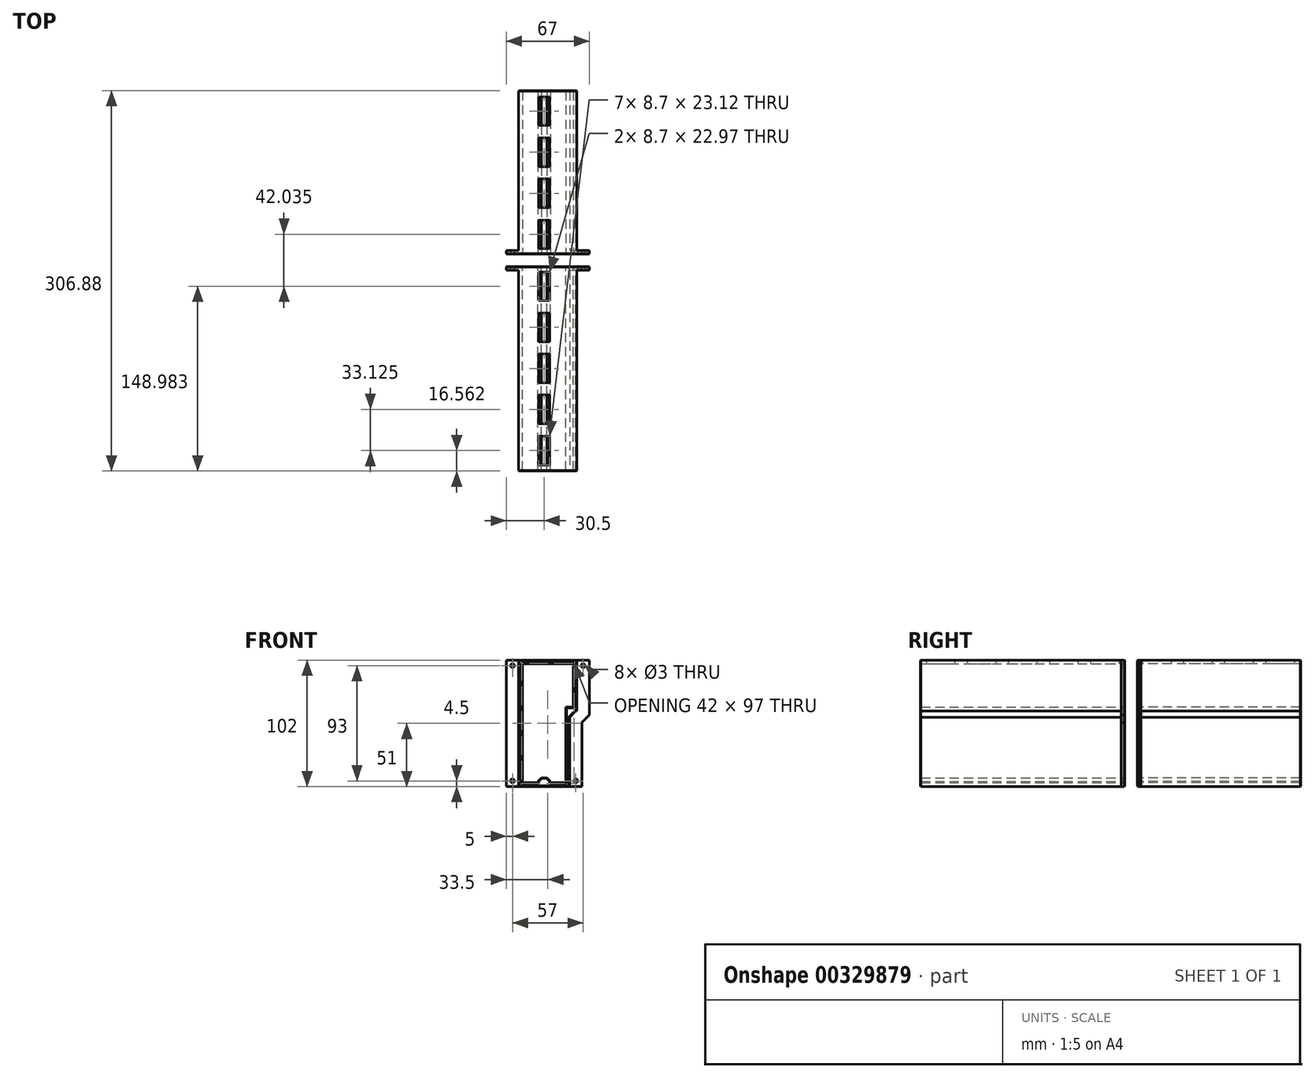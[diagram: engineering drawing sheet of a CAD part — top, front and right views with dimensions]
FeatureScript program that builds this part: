
annotation { "Feature Type Name" : "Feature", "Feature Type Description" : "" }
export const myFeature = defineFeature(function(context is Context, id is Id, definition is map)
    precondition{}
    {
        {
            var Q0;
            Q0=qCreatedBy(makeId("Front.planeOp"),FACE);
            var sketch = newSketch(context, id + "F0", { "sketchPlane" : qUnion([Q0])});
            skLineSegment(sketch, "E0", {"start": v(0, 0) * mm, "end": v(0, 1.2) * mm});
            skLineSegment(sketch, "E1", {"start": v(0, 1.2) * mm, "end": v(2.9, 4.1) * mm});
            skLineSegment(sketch, "E2", {"start": v(2.9, 4.1) * mm, "end": v(5, 4.1) * mm});
            skLineSegment(sketch, "E3", {"start": v(5, 4.1) * mm, "end": v(5, 0) * mm, "construction": true});
            skLineSegment(sketch, "E4", {"start": v(5, 0) * mm, "end": v(0, 0) * mm, "construction": true});
            skLineSegment(sketch, "E5", {"start": v(0, 0) * mm, "end": v(-12.5, 0) * mm});
            skLineSegment(sketch, "E6", {"start": v(-12.5, 0) * mm, "end": v(-12.5, 96) * mm});
            skLineSegment(sketch, "E7", {"start": v(-12.5, 96) * mm, "end": v(0.65, 96) * mm});
            skLineSegment(sketch, "E8", {"start": v(0.65, 96) * mm, "end": v(0.65, 99) * mm});
            skLineSegment(sketch, "E9", {"start": v(0.65, 99) * mm, "end": v(-15.5, 99) * mm});
            skLineSegment(sketch, "E10", {"start": v(-15.5, 99) * mm, "end": v(-15.5, -3) * mm});
            skLineSegment(sketch, "E11", {"start": v(-15.5, -3) * mm, "end": v(5, -3) * mm});
            skLineSegment(sketch, "E12", {"start": v(5, -3) * mm, "end": v(5, 0) * mm, "construction": true});
            skLineSegment(sketch, "E13.MirrorCS", {"start": v(7.1, 4.1) * mm, "end": v(5, 4.1) * mm});
            skLineSegment(sketch, "E14.MirrorCS", {"start": v(10, 1.2) * mm, "end": v(7.1, 4.1) * mm});
            skLineSegment(sketch, "E15.MirrorCS", {"start": v(10, 0) * mm, "end": v(10, 1.2) * mm});
            skLineSegment(sketch, "E16.MirrorCS", {"start": v(10, 0) * mm, "end": v(22.5, 0) * mm});
            skLineSegment(sketch, "E17.MirrorCS", {"start": v(22.5, 0) * mm, "end": v(22.5, 61) * mm});
            skLineSegment(sketch, "E18.MirrorCS", {"start": v(25.5, -3) * mm, "end": v(5, -3) * mm});
            skLineSegment(sketch, "E19.MirrorCS", {"start": v(9.35, 99) * mm, "end": v(31.5, 99) * mm});
            skLineSegment(sketch, "E20.MirrorCS", {"start": v(22.5, 96) * mm, "end": v(9.35, 96) * mm});
            skLineSegment(sketch, "E21.MirrorCS", {"start": v(9.35, 96) * mm, "end": v(9.35, 99) * mm});
            skLineSegment(sketch, "E22", {"start": v(22.5, 61) * mm, "end": v(28.5, 61) * mm});
            skLineSegment(sketch, "E23", {"start": v(28.5, 61) * mm, "end": v(28.5, 96) * mm});
            skLineSegment(sketch, "E24", {"start": v(28.5, 96) * mm, "end": v(22.5, 96) * mm});
            skLineSegment(sketch, "E25.0", {"start": v(31.5, 58) * mm, "end": v(31.5, 99) * mm});
            skLineSegment(sketch, "E25.1", {"start": v(25.5, 58) * mm, "end": v(31.5, 58) * mm});
            skLineSegment(sketch, "E25.2", {"start": v(25.5, -3) * mm, "end": v(25.5, 58) * mm});
            skSolve(sketch);
        }
        {
            var Q0;
            Q0 = qSketchRegion(id + "F0", true);
            extrude(context, id + "F1", {"entities" : qUnion([Q0]), "depth" : 165 * mm, "offsetDistance" : 25 * mm});
        }
        {
            var Q0;
            Q0=makeQuery(id+"F1.opExtrude","SWEPT_FACE",FACE,{"disambiguationData":[OSD([sQuery(id+"F0.wireOp",EDGE,"E9")])]});
            var sketch = newSketch(context, id + "F2", { "sketchPlane" : qUnion([Q0])});
            skLineSegment(sketch, "E26.bottom", {"start": v(0.65, -165) * mm, "end": v(9.35, -165) * mm});
            skLineSegment(sketch, "E26.top", {"start": v(0.65, -160) * mm, "end": v(9.35, -160) * mm});
            skLineSegment(sketch, "E26.left", {"start": v(0.65, -165) * mm, "end": v(0.65, -160) * mm});
            skLineSegment(sketch, "E26.right", {"start": v(9.35, -165) * mm, "end": v(9.35, -160) * mm});
            skLineSegment(sketch, "E27", {"start": v(0.65, -148.44) * mm, "end": v(9.35, -148.44) * mm, "construction": true});
            skLineSegment(sketch, "E28.bottom", {"start": v(0.65, -136.88) * mm, "end": v(9.35, -136.88) * mm});
            skLineSegment(sketch, "E28.top", {"start": v(0.65, -126.87) * mm, "end": v(9.35, -126.87) * mm});
            skLineSegment(sketch, "E28.left", {"start": v(0.65, -136.88) * mm, "end": v(0.65, -126.87) * mm});
            skLineSegment(sketch, "E28.right", {"start": v(9.35, -136.88) * mm, "end": v(9.35, -126.87) * mm});
            skLineSegment(sketch, "E29.0.1.0", {"start": v(0.65, -115.31) * mm, "end": v(9.35, -115.31) * mm, "construction": true});
            skLineSegment(sketch, "E29.0.1.1", {"start": v(0.65, -103.75) * mm, "end": v(9.35, -103.75) * mm});
            skLineSegment(sketch, "E29.0.1.2", {"start": v(0.65, -103.75) * mm, "end": v(0.65, -93.75) * mm});
            skLineSegment(sketch, "E29.0.1.3", {"start": v(0.65, -93.75) * mm, "end": v(9.35, -93.75) * mm});
            skLineSegment(sketch, "E29.0.1.4", {"start": v(9.35, -103.75) * mm, "end": v(9.35, -93.75) * mm});
            skLineSegment(sketch, "E29.direction2", {"start": v(0.65, -148.44) * mm, "end": v(0.65, -115.31) * mm, "construction": true});
            skLineSegment(sketch, "E30", {"start": v(0.65, -131.88) * mm, "end": v(0.65, -115.31) * mm});
            skLineSegment(sketch, "E31", {"start": v(0.65, -131.88) * mm, "end": v(0.65, -148.44) * mm});
            skLineSegment(sketch, "E32.0.0.2", {"start": v(0.65, -82.19) * mm, "end": v(9.35, -82.19) * mm, "construction": true});
            skLineSegment(sketch, "E32.3.0.2", {"start": v(0.65, -70.63) * mm, "end": v(9.35, -70.63) * mm});
            skLineSegment(sketch, "E32.6.0.2", {"start": v(0.65, -70.63) * mm, "end": v(0.65, -60.63) * mm});
            skLineSegment(sketch, "E32.9.0.2", {"start": v(0.65, -60.63) * mm, "end": v(9.35, -60.63) * mm});
            skLineSegment(sketch, "E32.12.0.2", {"start": v(9.35, -70.63) * mm, "end": v(9.35, -60.63) * mm});
            skLineSegment(sketch, "E32.0.0.3", {"start": v(0.65, -49.06) * mm, "end": v(9.35, -49.06) * mm, "construction": true});
            skLineSegment(sketch, "E32.3.0.3", {"start": v(0.65, -37.5) * mm, "end": v(9.35, -37.5) * mm});
            skLineSegment(sketch, "E32.6.0.3", {"start": v(0.65, -37.5) * mm, "end": v(0.65, -27.5) * mm});
            skLineSegment(sketch, "E32.9.0.3", {"start": v(0.65, -27.5) * mm, "end": v(9.35, -27.5) * mm});
            skLineSegment(sketch, "E32.12.0.3", {"start": v(9.35, -37.5) * mm, "end": v(9.35, -27.5) * mm});
            skLineSegment(sketch, "E33.0.0.4", {"start": v(0.65, -15.94) * mm, "end": v(9.35, -15.94) * mm, "construction": true});
            skLineSegment(sketch, "E33.3.0.4", {"start": v(0.65, -4.53) * mm, "end": v(9.35, -4.53) * mm});
            skLineSegment(sketch, "E33.6.0.4", {"start": v(0.65, -4.53) * mm, "end": v(0.65, 0) * mm});
            skLineSegment(sketch, "E33.9.0.4", {"start": v(0.65, 0) * mm, "end": v(9.35, 0) * mm});
            skLineSegment(sketch, "E33.12.0.4", {"start": v(9.35, -4.53) * mm, "end": v(9.35, 0) * mm});
            skSolve(sketch);
        }
        {
            var Q0;
            Q0 = qSketchRegion(id + "F2", true);
            var Q1;
            Q1=makeQuery(id+"F1.opExtrude","SWEPT_FACE",FACE,{"disambiguationData":[OSD([sQuery(id+"F0.wireOp",EDGE,"E7")])]});
            extrude(context, id + "F3", {"entities" : qUnion([Q0]), "operationType" : NewBodyOperationType.ADD, "endBound" : BoundingType.UP_TO_SURFACE, "oppositeDirection" : true, "depth" : 25 * mm, "endBoundEntityFace" : qUnion([Q1]), "offsetDistance" : 25 * mm});
        }
        {
            var Q0;
            Q0=makeQuery(id+"F1.opExtrude","SWEPT_EDGE",EDGE,{"disambiguationData":[OSD([sQuery(id+"F0.wireOp",EDGE,"E25.1"),sQuery(id+"F0.wireOp",EDGE,"E25.2")])]});
            chamfer(context, id + "F4", {"entities" : qUnion([Q0]), "width" : 5 * mm, "tangentPropagation" : true});
        }
        {
            var Q0;
            Q0=makeQuery(id+"F3.boolean.opBoolean","MERGE",FACE,{"derivedFrom":[makeQuery(id+"F1.opExtrude","CAP_FACE",FACE,{"disambiguationData":[OSD([sQuery(id+"F0.wireOp",EDGE,"E0"),sQuery(id+"F0.wireOp",EDGE,"E1"),sQuery(id+"F0.wireOp",EDGE,"E2"),sQuery(id+"F0.wireOp",EDGE,"E5"),sQuery(id+"F0.wireOp",EDGE,"E6"),sQuery(id+"F0.wireOp",EDGE,"E7"),sQuery(id+"F0.wireOp",EDGE,"E8"),sQuery(id+"F0.wireOp",EDGE,"E9"),sQuery(id+"F0.wireOp",EDGE,"E10"),sQuery(id+"F0.wireOp",EDGE,"E11"),sQuery(id+"F0.wireOp",EDGE,"E13.MirrorCS"),sQuery(id+"F0.wireOp",EDGE,"E14.MirrorCS"),sQuery(id+"F0.wireOp",EDGE,"E15.MirrorCS"),sQuery(id+"F0.wireOp",EDGE,"E16.MirrorCS"),sQuery(id+"F0.wireOp",EDGE,"E17.MirrorCS"),sQuery(id+"F0.wireOp",EDGE,"E18.MirrorCS"),sQuery(id+"F0.wireOp",EDGE,"E19.MirrorCS"),sQuery(id+"F0.wireOp",EDGE,"E20.MirrorCS"),sQuery(id+"F0.wireOp",EDGE,"E21.MirrorCS"),sQuery(id+"F0.wireOp",EDGE,"E22"),sQuery(id+"F0.wireOp",EDGE,"E23"),sQuery(id+"F0.wireOp",EDGE,"E24"),sQuery(id+"F0.wireOp",EDGE,"E25.0"),sQuery(id+"F0.wireOp",EDGE,"E25.1"),sQuery(id+"F0.wireOp",EDGE,"E25.2")])],"isStart":true}),makeQuery(id+"F3.opExtrude","SWEPT_FACE",FACE,{"disambiguationData":[OSD([sQuery(id+"F2.wireOp",EDGE,"E33.9.0.4")])]})]});
            var sketch = newSketch(context, id + "F5", { "sketchPlane" : qUnion([Q0])});
            skLineSegment(sketch, "E34.0", {"start": v(-22.5, 61) * mm, "end": v(-28.5, 61) * mm});
            skLineSegment(sketch, "E34.1", {"start": v(0, 0) * mm, "end": v(0, 1.2) * mm});
            skLineSegment(sketch, "E34.2", {"start": v(0, 0) * mm, "end": v(12.5, 0) * mm});
            skLineSegment(sketch, "E34.3", {"start": v(12.5, 0) * mm, "end": v(12.5, 96) * mm});
            skLineSegment(sketch, "E34.4", {"start": v(-28.5, 96) * mm, "end": v(12.5, 96) * mm});
            skLineSegment(sketch, "E34.5", {"start": v(0, 1.2) * mm, "end": v(-2.9, 4.1) * mm});
            skLineSegment(sketch, "E34.6", {"start": v(-28.5, 61) * mm, "end": v(-28.5, 96) * mm});
            skLineSegment(sketch, "E34.7", {"start": v(-2.9, 4.1) * mm, "end": v(-7.1, 4.1) * mm});
            skLineSegment(sketch, "E34.8", {"start": v(-10, 1.2) * mm, "end": v(-7.1, 4.1) * mm});
            skLineSegment(sketch, "E34.9", {"start": v(-10, 0) * mm, "end": v(-10, 1.2) * mm});
            skLineSegment(sketch, "E34.10", {"start": v(-10, 0) * mm, "end": v(-22.5, 0) * mm});
            skLineSegment(sketch, "E34.11", {"start": v(-22.5, 0) * mm, "end": v(-22.5, 61) * mm});
            skLineSegment(sketch, "E35.0", {"start": v(25.5, 99) * mm, "end": v(25.5, -3) * mm});
            skLineSegment(sketch, "E35.1", {"start": v(-35.5, -3) * mm, "end": v(-35.5, 48.86) * mm});
            skLineSegment(sketch, "E35.2", {"start": v(-41.5, 54.86) * mm, "end": v(-35.5, 48.86) * mm});
            skLineSegment(sketch, "E35.3", {"start": v(-41.5, 54.86) * mm, "end": v(-41.5, 99) * mm});
            skLineSegment(sketch, "E35.4", {"start": v(25.5, 99) * mm, "end": v(-41.5, 99) * mm});
            skLineSegment(sketch, "E36", {"start": v(-35.5, -3) * mm, "end": v(25.5, -3) * mm});
            skCircle(sketch, "E37", {"center": v(-30.5, 1.5) * mm, "radius": 1.5 * mm});
            skCircle(sketch, "E38", {"center": v(-36.5, 94.5) * mm, "radius": 1.5 * mm});
            skCircle(sketch, "E39", {"center": v(20.5, 94.5) * mm, "radius": 1.5 * mm});
            skCircle(sketch, "E40", {"center": v(20.5, 1.5) * mm, "radius": 1.5 * mm});
            skLineSegment(sketch, "E41", {"start": v(-35.5, 1.5) * mm, "end": v(-30.5, 1.5) * mm, "construction": true});
            skLineSegment(sketch, "E42", {"start": v(-30.5, 1.5) * mm, "end": v(-25.5, 1.5) * mm, "construction": true});
            skLineSegment(sketch, "E43", {"start": v(15.5, 1.5) * mm, "end": v(20.5, 1.5) * mm, "construction": true});
            skLineSegment(sketch, "E44", {"start": v(20.5, 1.5) * mm, "end": v(25.5, 1.5) * mm, "construction": true});
            skLineSegment(sketch, "E45", {"start": v(-31.5, 94.5) * mm, "end": v(-41.5, 94.5) * mm, "construction": true});
            skLineSegment(sketch, "E46", {"start": v(15.5, 94.5) * mm, "end": v(25.5, 94.5) * mm, "construction": true});
            skSolve(sketch);
        }
        {
            var Q0;
            Q0 = qSketchRegion(id + "F5", true);
            extrude(context, id + "F6", {"entities" : qUnion([Q0]), "operationType" : NewBodyOperationType.ADD, "oppositeDirection" : true, "depth" : 3 * mm, "offsetDistance" : 25 * mm});
        }
        {
            var Q0;
            {var subQ0=makeQuery(id+"F1.opExtrude","CAP_FACE",FACE,{"disambiguationData":[OSD([sQuery(id+"F0.wireOp",EDGE,"E0"),sQuery(id+"F0.wireOp",EDGE,"E1"),sQuery(id+"F0.wireOp",EDGE,"E2"),sQuery(id+"F0.wireOp",EDGE,"E3"),sQuery(id+"F0.wireOp",EDGE,"E5"),sQuery(id+"F0.wireOp",EDGE,"E6"),sQuery(id+"F0.wireOp",EDGE,"E7"),sQuery(id+"F0.wireOp",EDGE,"E8"),sQuery(id+"F0.wireOp",EDGE,"E9"),sQuery(id+"F0.wireOp",EDGE,"E10"),sQuery(id+"F0.wireOp",EDGE,"E11"),sQuery(id+"F0.wireOp",EDGE,"E12")])],"isStart":true});Q0=makeQuery(id+"F2d3Ql1Mtt5XJC1_1.boolean.opBoolean","MERGE",FACE,{"derivedFrom":[subQ0,makeQuery(id+"F2d3Ql1Mtt5XJC1_1.opPattern","COPY",FACE,{"derivedFrom":subQ0,"instanceName":"1"})]});}
            var Q1;
            {var subQ0=makeQuery(id+"F1.opExtrude","CAP_FACE",FACE,{"disambiguationData":[OSD([sQuery(id+"F0.wireOp",EDGE,"E0"),sQuery(id+"F0.wireOp",EDGE,"E1"),sQuery(id+"F0.wireOp",EDGE,"E2"),sQuery(id+"F0.wireOp",EDGE,"E3"),sQuery(id+"F0.wireOp",EDGE,"E5"),sQuery(id+"F0.wireOp",EDGE,"E6"),sQuery(id+"F0.wireOp",EDGE,"E7"),sQuery(id+"F0.wireOp",EDGE,"E8"),sQuery(id+"F0.wireOp",EDGE,"E9"),sQuery(id+"F0.wireOp",EDGE,"E10"),sQuery(id+"F0.wireOp",EDGE,"E11"),sQuery(id+"F0.wireOp",EDGE,"E12")])],"isStart":false});Q1=makeQuery(id+"F2d3Ql1Mtt5XJC1_1.boolean.opBoolean","MERGE",FACE,{"derivedFrom":[subQ0,makeQuery(id+"F2d3Ql1Mtt5XJC1_1.opPattern","COPY",FACE,{"derivedFrom":subQ0,"instanceName":"1"})]});}
            chamfer(context, id + "F7", {"entities" : qUnion([Q0, Q1]), "width" : 0.5 * mm, "tangentPropagation" : true});
        }
        {
            var Q0;
            Q0=makeQuery(id+"F6.boolean.opBoolean","MERGE",FACE,{"derivedFrom":[makeQuery(id+"F3.boolean.opBoolean","MERGE",FACE,{"derivedFrom":[makeQuery(id+"F1.opExtrude","CAP_FACE",FACE,{"disambiguationData":[OSD([sQuery(id+"F0.wireOp",EDGE,"E0"),sQuery(id+"F0.wireOp",EDGE,"E1"),sQuery(id+"F0.wireOp",EDGE,"E2"),sQuery(id+"F0.wireOp",EDGE,"E5"),sQuery(id+"F0.wireOp",EDGE,"E6"),sQuery(id+"F0.wireOp",EDGE,"E7"),sQuery(id+"F0.wireOp",EDGE,"E8"),sQuery(id+"F0.wireOp",EDGE,"E9"),sQuery(id+"F0.wireOp",EDGE,"E10"),sQuery(id+"F0.wireOp",EDGE,"E11"),sQuery(id+"F0.wireOp",EDGE,"E13.MirrorCS"),sQuery(id+"F0.wireOp",EDGE,"E14.MirrorCS"),sQuery(id+"F0.wireOp",EDGE,"E15.MirrorCS"),sQuery(id+"F0.wireOp",EDGE,"E16.MirrorCS"),sQuery(id+"F0.wireOp",EDGE,"E17.MirrorCS"),sQuery(id+"F0.wireOp",EDGE,"E18.MirrorCS"),sQuery(id+"F0.wireOp",EDGE,"E19.MirrorCS"),sQuery(id+"F0.wireOp",EDGE,"E20.MirrorCS"),sQuery(id+"F0.wireOp",EDGE,"E21.MirrorCS"),sQuery(id+"F0.wireOp",EDGE,"E22"),sQuery(id+"F0.wireOp",EDGE,"E23"),sQuery(id+"F0.wireOp",EDGE,"E24"),sQuery(id+"F0.wireOp",EDGE,"E25.0"),sQuery(id+"F0.wireOp",EDGE,"E25.1"),sQuery(id+"F0.wireOp",EDGE,"E25.2")])],"isStart":true}),makeQuery(id+"F3.opExtrude","SWEPT_FACE",FACE,{"disambiguationData":[OSD([sQuery(id+"F2.wireOp",EDGE,"E33.9.0.4")])]})]}),makeQuery(id+"F6.opExtrude","CAP_FACE",FACE,{"disambiguationData":[OSD([sQuery(id+"F5.wireOp",EDGE,"E34.0"),sQuery(id+"F5.wireOp",EDGE,"E34.1"),sQuery(id+"F5.wireOp",EDGE,"E34.2"),sQuery(id+"F5.wireOp",EDGE,"E34.3"),sQuery(id+"F5.wireOp",EDGE,"E34.4"),sQuery(id+"F5.wireOp",EDGE,"E34.5"),sQuery(id+"F5.wireOp",EDGE,"E34.6"),sQuery(id+"F5.wireOp",EDGE,"E34.7"),sQuery(id+"F5.wireOp",EDGE,"E34.8"),sQuery(id+"F5.wireOp",EDGE,"E34.9"),sQuery(id+"F5.wireOp",EDGE,"E34.10"),sQuery(id+"F5.wireOp",EDGE,"E34.11"),sQuery(id+"F5.wireOp",EDGE,"E35.0"),sQuery(id+"F5.wireOp",EDGE,"E35.1"),sQuery(id+"F5.wireOp",EDGE,"E35.2"),sQuery(id+"F5.wireOp",EDGE,"E35.3"),sQuery(id+"F5.wireOp",EDGE,"E35.4"),sQuery(id+"F5.wireOp",EDGE,"E36"),sQuery(id+"F5.wireOp",EDGE,"E37"),sQuery(id+"F5.wireOp",EDGE,"E38"),sQuery(id+"F5.wireOp",EDGE,"E39"),sQuery(id+"F5.wireOp",EDGE,"E40")])],"isStart":true})]});
            cPlane(context, id + "F8", {"entities" : qUnion([Q0]), "cplaneType" : CPlaneType.OFFSET, "offset" : 5 * mm, "width" : 150 * mm, "height" : 150 * mm});
        }
        {
            var Q0;
            Q0=makeQuery(id+"F1.opExtrude","SWEPT_BODY",BODY,{"disambiguationData":[OSD([sQuery(id+"F0.wireOp",EDGE,"E0"),sQuery(id+"F0.wireOp",EDGE,"E1"),sQuery(id+"F0.wireOp",EDGE,"E2"),sQuery(id+"F0.wireOp",EDGE,"E5"),sQuery(id+"F0.wireOp",EDGE,"E6"),sQuery(id+"F0.wireOp",EDGE,"E7"),sQuery(id+"F0.wireOp",EDGE,"E8"),sQuery(id+"F0.wireOp",EDGE,"E9"),sQuery(id+"F0.wireOp",EDGE,"E10"),sQuery(id+"F0.wireOp",EDGE,"E11"),sQuery(id+"F0.wireOp",EDGE,"E13.MirrorCS"),sQuery(id+"F0.wireOp",EDGE,"E14.MirrorCS"),sQuery(id+"F0.wireOp",EDGE,"E15.MirrorCS"),sQuery(id+"F0.wireOp",EDGE,"E16.MirrorCS"),sQuery(id+"F0.wireOp",EDGE,"E17.MirrorCS"),sQuery(id+"F0.wireOp",EDGE,"E18.MirrorCS"),sQuery(id+"F0.wireOp",EDGE,"E19.MirrorCS"),sQuery(id+"F0.wireOp",EDGE,"E20.MirrorCS"),sQuery(id+"F0.wireOp",EDGE,"E21.MirrorCS"),sQuery(id+"F0.wireOp",EDGE,"E22"),sQuery(id+"F0.wireOp",EDGE,"E23"),sQuery(id+"F0.wireOp",EDGE,"E24"),sQuery(id+"F0.wireOp",EDGE,"E25.0"),sQuery(id+"F0.wireOp",EDGE,"E25.1"),sQuery(id+"F0.wireOp",EDGE,"E25.2")])]});
            var Q1;
            Q1=qCreatedBy(id+"F8.planeOp",FACE);
            mirror(context, id + "F9", {"entities" : qUnion([Q0]), "mirrorPlane" : qUnion([Q1])});
        }
        {
            var Q0;
            Q0=makeQuery(id+"F9.opPattern","COPY",FACE,{"derivedFrom":makeQuery(id+"F3.opExtrude","SWEPT_FACE",FACE,{"disambiguationData":[OSD([sQuery(id+"F2.wireOp",EDGE,"E28.bottom")])]}),"instanceName":"1"});
            var Q1;
            Q1=makeQuery(id+"F9.opPattern","COPY",FACE,{"derivedFrom":makeQuery(id+"F3.opExtrude","SWEPT_FACE",FACE,{"disambiguationData":[OSD([sQuery(id+"F2.wireOp",EDGE,"E28.top")])]}),"instanceName":"1"});
            cPlane(context, id + "F10", {"entities" : qUnion([Q0, Q1]), "cplaneType" : CPlaneType.MID_PLANE, "offset" : 25 * mm, "width" : 150 * mm, "height" : 150 * mm});
        }
        {
            var Q0;
            Q0=makeQuery(id+"F9.opPattern","COPY",FACE,{"derivedFrom":makeQuery(id+"F3.boolean.opBoolean","MERGE",FACE,{"derivedFrom":[makeQuery(id+"F1.opExtrude","CAP_FACE",FACE,{"disambiguationData":[OSD([sQuery(id+"F0.wireOp",EDGE,"E0"),sQuery(id+"F0.wireOp",EDGE,"E1"),sQuery(id+"F0.wireOp",EDGE,"E2"),sQuery(id+"F0.wireOp",EDGE,"E5"),sQuery(id+"F0.wireOp",EDGE,"E6"),sQuery(id+"F0.wireOp",EDGE,"E7"),sQuery(id+"F0.wireOp",EDGE,"E8"),sQuery(id+"F0.wireOp",EDGE,"E9"),sQuery(id+"F0.wireOp",EDGE,"E10"),sQuery(id+"F0.wireOp",EDGE,"E11"),sQuery(id+"F0.wireOp",EDGE,"E13.MirrorCS"),sQuery(id+"F0.wireOp",EDGE,"E14.MirrorCS"),sQuery(id+"F0.wireOp",EDGE,"E15.MirrorCS"),sQuery(id+"F0.wireOp",EDGE,"E16.MirrorCS"),sQuery(id+"F0.wireOp",EDGE,"E17.MirrorCS"),sQuery(id+"F0.wireOp",EDGE,"E18.MirrorCS"),sQuery(id+"F0.wireOp",EDGE,"E19.MirrorCS"),sQuery(id+"F0.wireOp",EDGE,"E20.MirrorCS"),sQuery(id+"F0.wireOp",EDGE,"E21.MirrorCS"),sQuery(id+"F0.wireOp",EDGE,"E22"),sQuery(id+"F0.wireOp",EDGE,"E23"),sQuery(id+"F0.wireOp",EDGE,"E24"),sQuery(id+"F0.wireOp",EDGE,"E25.0"),sQuery(id+"F0.wireOp",EDGE,"E25.1"),sQuery(id+"F0.wireOp",EDGE,"E25.2")])],"isStart":false}),makeQuery(id+"F3.opExtrude","SWEPT_FACE",FACE,{"disambiguationData":[OSD([sQuery(id+"F2.wireOp",EDGE,"E26.bottom")])]})]}),"instanceName":"1"});
            var sketch = newSketch(context, id + "F11", { "sketchPlane" : qUnion([Q0])});
            skLineSegment(sketch, "E47.0", {"start": v(20.5, -8) * mm, "end": v(20.5, 104) * mm});
            skLineSegment(sketch, "E47.1", {"start": v(-36.5, 104) * mm, "end": v(-36.5, 56.93) * mm});
            skLineSegment(sketch, "E47.2", {"start": v(-36.5, 56.93) * mm, "end": v(-30.5, 50.93) * mm});
            skLineSegment(sketch, "E47.3", {"start": v(20.5, 104) * mm, "end": v(-36.5, 104) * mm});
            skLineSegment(sketch, "E47.4", {"start": v(-30.5, 50.93) * mm, "end": v(-30.5, -8) * mm});
            skLineSegment(sketch, "E47.5", {"start": v(-30.5, -8) * mm, "end": v(20.5, -8) * mm});
            skSolve(sketch);
        }
        {
            var Q0;
            Q0 = qSketchRegion(id + "F11", true);
            var Q1;
            Q1=qCreatedBy(id+"F10.planeOp",FACE);
            extrude(context, id + "F12", {"entities" : qUnion([Q0]), "operationType" : NewBodyOperationType.REMOVE, "endBound" : BoundingType.UP_TO_SURFACE, "oppositeDirection" : true, "depth" : 25 * mm, "endBoundEntityFace" : qUnion([Q1]), "offsetDistance" : 25 * mm});
        }
        {
            var Q0;
            Q0=makeQuery(id+"F12.boolean.opBoolean","COPY",FACE,{"derivedFrom":makeQuery(id+"F12.opExtrude","CAP_FACE",FACE,{"disambiguationData":[OSD([sQuery(id+"F11.wireOp",EDGE,"E47.0"),sQuery(id+"F11.wireOp",EDGE,"E47.1"),sQuery(id+"F11.wireOp",EDGE,"E47.2"),sQuery(id+"F11.wireOp",EDGE,"E47.3"),sQuery(id+"F11.wireOp",EDGE,"E47.4"),sQuery(id+"F11.wireOp",EDGE,"E47.5")])],"isStart":false})});
            chamfer(context, id + "F13", {"entities" : qUnion([Q0]), "width" : 0.4 * mm, "tangentPropagation" : true});
        }
    });
